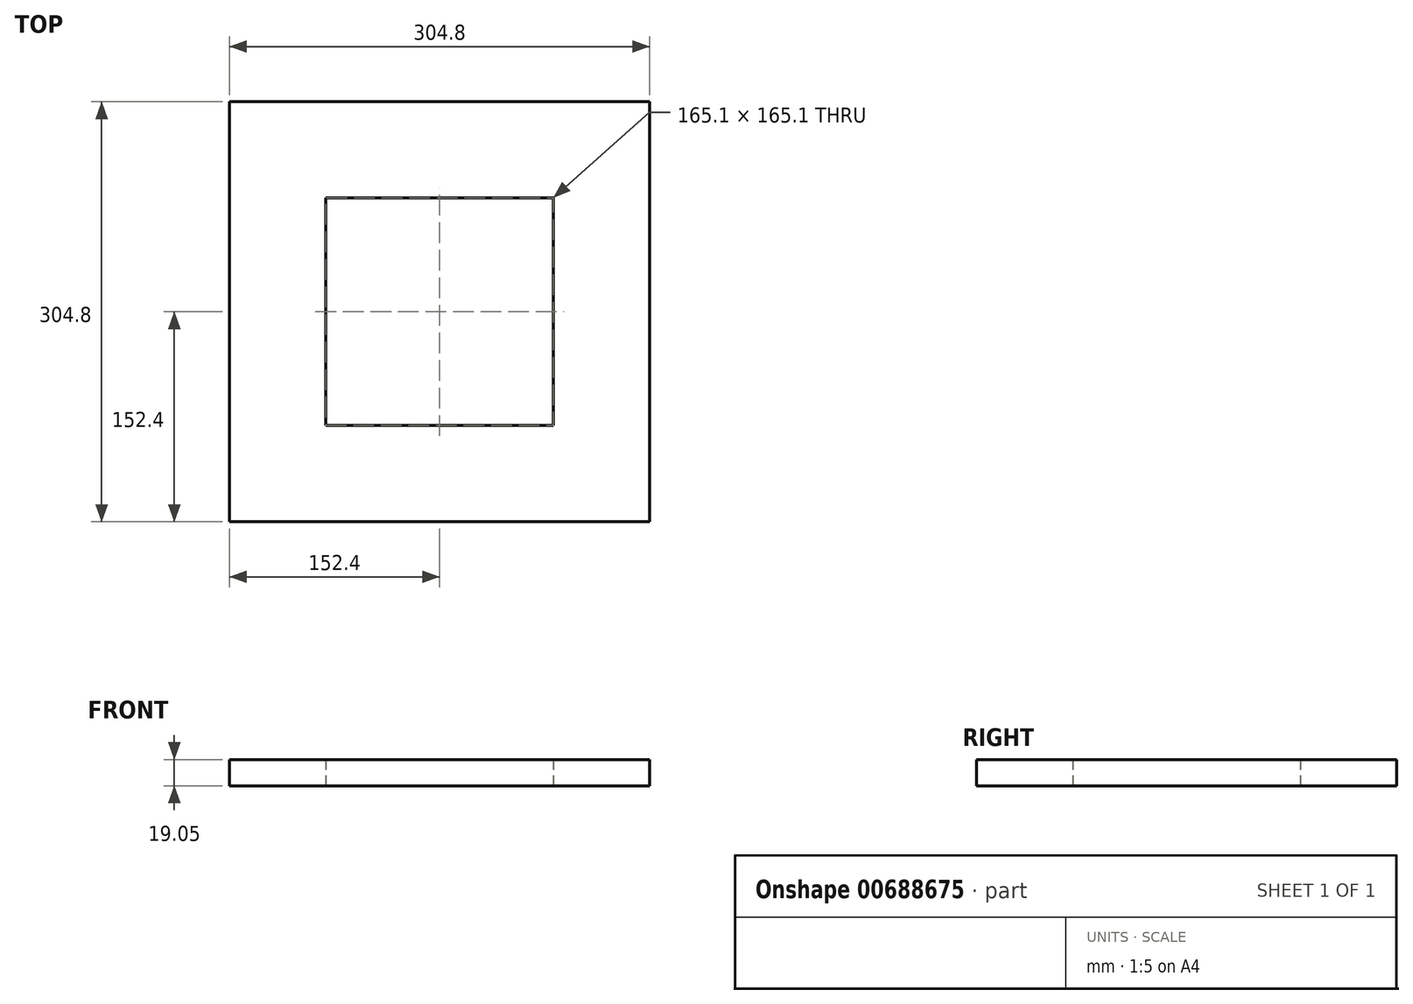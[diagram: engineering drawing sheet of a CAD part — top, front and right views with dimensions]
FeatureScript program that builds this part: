
annotation { "Feature Type Name" : "Feature", "Feature Type Description" : "" }
export const myFeature = defineFeature(function(context is Context, id is Id, definition is map)
    precondition{}
    {
        {
            var Q0;
            Q0=qCreatedBy(makeId("Top.planeOp"),FACE);
            var sketch = newSketch(context, id + "F0", { "sketchPlane" : qUnion([Q0])});
            skLineSegment(sketch, "E0.bottom", {"start": v(-152.4, 152.4) * mm, "end": v(152.4, 152.4) * mm});
            skLineSegment(sketch, "E0.top", {"start": v(-152.4, -152.4) * mm, "end": v(152.4, -152.4) * mm});
            skLineSegment(sketch, "E0.left", {"start": v(-152.4, 152.4) * mm, "end": v(-152.4, -152.4) * mm});
            skLineSegment(sketch, "E0.right", {"start": v(152.4, 152.4) * mm, "end": v(152.4, -152.4) * mm});
            skPoint(sketch, "E0.middle", {"position": v(0, 0) * mm});
            skLineSegment(sketch, "E1.bottom", {"start": v(-82.55, 82.55) * mm, "end": v(82.55, 82.55) * mm});
            skLineSegment(sketch, "E1.top", {"start": v(-82.55, -82.55) * mm, "end": v(82.55, -82.55) * mm});
            skLineSegment(sketch, "E1.left", {"start": v(-82.55, 82.55) * mm, "end": v(-82.55, -82.55) * mm});
            skLineSegment(sketch, "E1.right", {"start": v(82.55, 82.55) * mm, "end": v(82.55, -82.55) * mm});
            skSolve(sketch);
        }
        {
            var Q0;
            Q0=makeQuery(id+"F0.imprint","IMPRINT",FACE,{"disambiguationData":[TD([[makeQuery(id+"F0.imprint","IMPRINT",EDGE,{"derivedFrom":sQuery(id+"F0.wireOp",EDGE,"E0.bottom")}),-1.0]])]});
            extrude(context, id + "F1", {"entities" : qUnion([Q0]), "depth" : 19.05 * mm, "offsetDistance" : 25.4 * mm});
        }
    });
